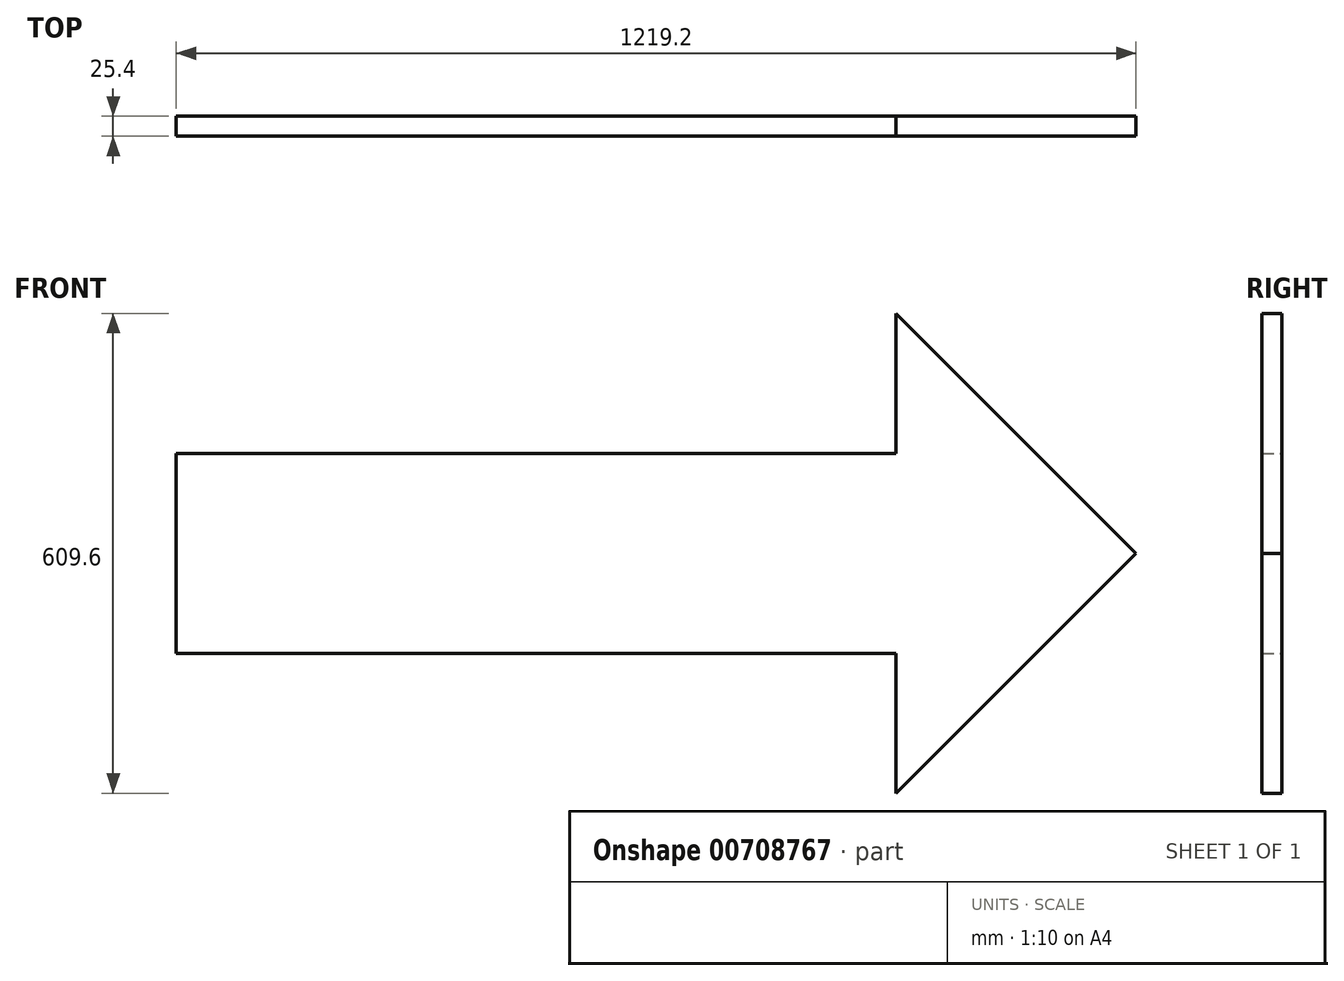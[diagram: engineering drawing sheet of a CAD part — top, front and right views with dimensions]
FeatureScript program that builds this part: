
annotation { "Feature Type Name" : "Feature", "Feature Type Description" : "" }
export const myFeature = defineFeature(function(context is Context, id is Id, definition is map)
    precondition{}
    {
        {
            var Q0;
            Q0=qCreatedBy(makeId("Front.planeOp"),FACE);
            var sketch = newSketch(context, id + "F0", { "sketchPlane" : qUnion([Q0])});
            skLineSegment(sketch, "E0", {"start": v(0, 0) * mm, "end": v(914.4, 0) * mm});
            skLineSegment(sketch, "E1", {"start": v(914.4, 0) * mm, "end": v(914.4, -177.8) * mm});
            skLineSegment(sketch, "E2", {"start": v(914.4, -177.8) * mm, "end": v(1219.2, 127) * mm});
            skLineSegment(sketch, "E3", {"start": v(1219.2, 127) * mm, "end": v(914.4, 431.8) * mm});
            skLineSegment(sketch, "E4", {"start": v(914.4, 431.8) * mm, "end": v(914.4, 254) * mm});
            skLineSegment(sketch, "E5", {"start": v(914.4, 254) * mm, "end": v(0, 254) * mm});
            skLineSegment(sketch, "E6", {"start": v(0, 254) * mm, "end": v(0, 0) * mm});
            skPoint(sketch, "E7", {"position": v(0, 127) * mm});
            skSolve(sketch);
        }
        {
            var Q0;
            Q0 = qSketchRegion(id + "F0", true);
            extrude(context, id + "F1", {"entities" : qUnion([Q0]), "depth" : 25.4 * mm, "offsetDistance" : 25.4 * mm});
        }
    });
